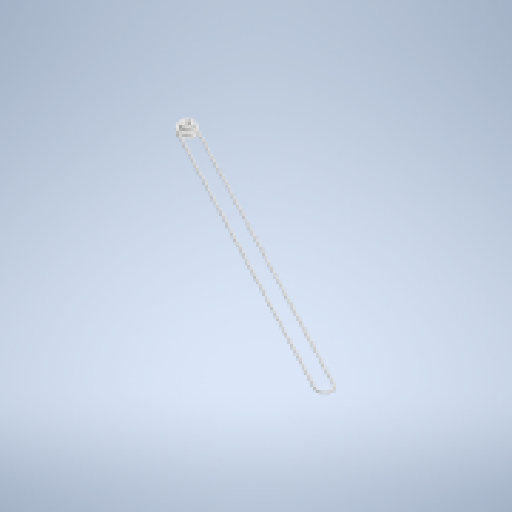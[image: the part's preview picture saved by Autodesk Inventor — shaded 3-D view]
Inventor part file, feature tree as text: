
AUTODESK INVENTOR PART (.ipt)
format: ipt  version: 2024 (Build 280153000, 153)  size: 231,424 bytes
history: native  units: in
note: dims shown in document units (in); Inventor stores cm internally (conversion verified against a paired STEP export)
features: chamfer x1, sweep x1
ambient origin geometry x8: Origin, YZ Plane, XZ Plane, XY Plane, X Axis, Y Axis, Z Axis, Center Point
bodies: Solid1 (feature_tree), Solid2 (feature_tree)
feature tree (2):
  chamfer  "Chamfer1"  [1 undecoded]
  sweep  "Sweep1"
note: 1 required parameter value undecoded (feature->parameter linkage not recoverable at this tier; creation-order binding heuristic only, values carry confidence <= 0.55)
